# Revit family: Дверь ОД1
name_source: partatom
category: Двери
revit_build: Autodesk Revit 2015 (Build: 20140223_1515(x64)
units: mm (PartAtom-declared; Revit-internal decimal feet)

## types (1)
- Дверь ОД1
    ADSK_URL страницы изделия = http://profholod.ru
    ADSK_Завод-изготовитель = ООО ПрофХолод
    ADSK_Наименование = ОД 1200 2300 ,,.,
    ADSK_Обозначение = ООО ПрофХолод
    ADSK_Открывание = Пр
    AISI = AISI430
    H_bottom_ door = 35 мм
    L_bottom = 1 мм
    L_top = 0 мм
    L_top_b = -1 мм
    RAL = RAL
    R_bottom = 1425 мм
    R_top = 1375 мм
    R_top_b = 1375 мм
    Shift_door = 77 мм
    URL = http://profholod.ru
    Аналитическая конструкция = <Нет>
    Верхняя фасонка длина = 240 мм
    Внутренняя сторона = RAL9003
    Высота = 2100 мм
    Высота в свету = 2100 мм
    Высота порога = 0 мм
    Высота проема до монтажа = 2100 мм
    Высота ручек = 1000 мм
    Группа модели = ОД
    Замыкание стены = По основе
    Изготовитель = ООО ПрофХолод
    Изогнутый отбойник левый = Нет
    Изогнутый отбойник правый = Нет
    Коробка и наличники = RAL9003
    Левая легкая = Нет
    Левая тяжелая = Нет
    Легкая дверь = Да
    НЕТ = НЕТ
    Наружная сторона = RAL9003
    Описание = Двери откатные (ОД)
    Петли левые = Нет
    Петли правые = Да
    Порог = Нет
    Правая легкая = Да
    Правая тяжелая = Нет
    Резиновые изделия = Резина
    ТК_КРК = ККС : КРК - к крипичной стене
    ТК_МК = ККС : МК - к металлоконструкции
    ТК_СП = ККС : СП - к сэндвич-панели
    Тип отбойника = Нет
    Толщина полотна = 120 мм
    Тяжелая = Нет
    Функция = Внутренние слои
    Фурнитура = Пластмасса, непрозрачная, черная
    Фурнитура сталь = AISI 430-0,5
    Ширина = 1250 мм
    Ширина в свету = 1000 мм
    Ширина проема до монтажа = 1250 мм
    Ширина рамы = 150 мм
    пНЕРЖ = Порог : AISI430
    пНЕТ = Порог : NULL
    пРАЛ = Порог : RAL 9003

## geometry (parser evidence)
native form markers: Sweep x3
no freeform markers — native parametric forms only
